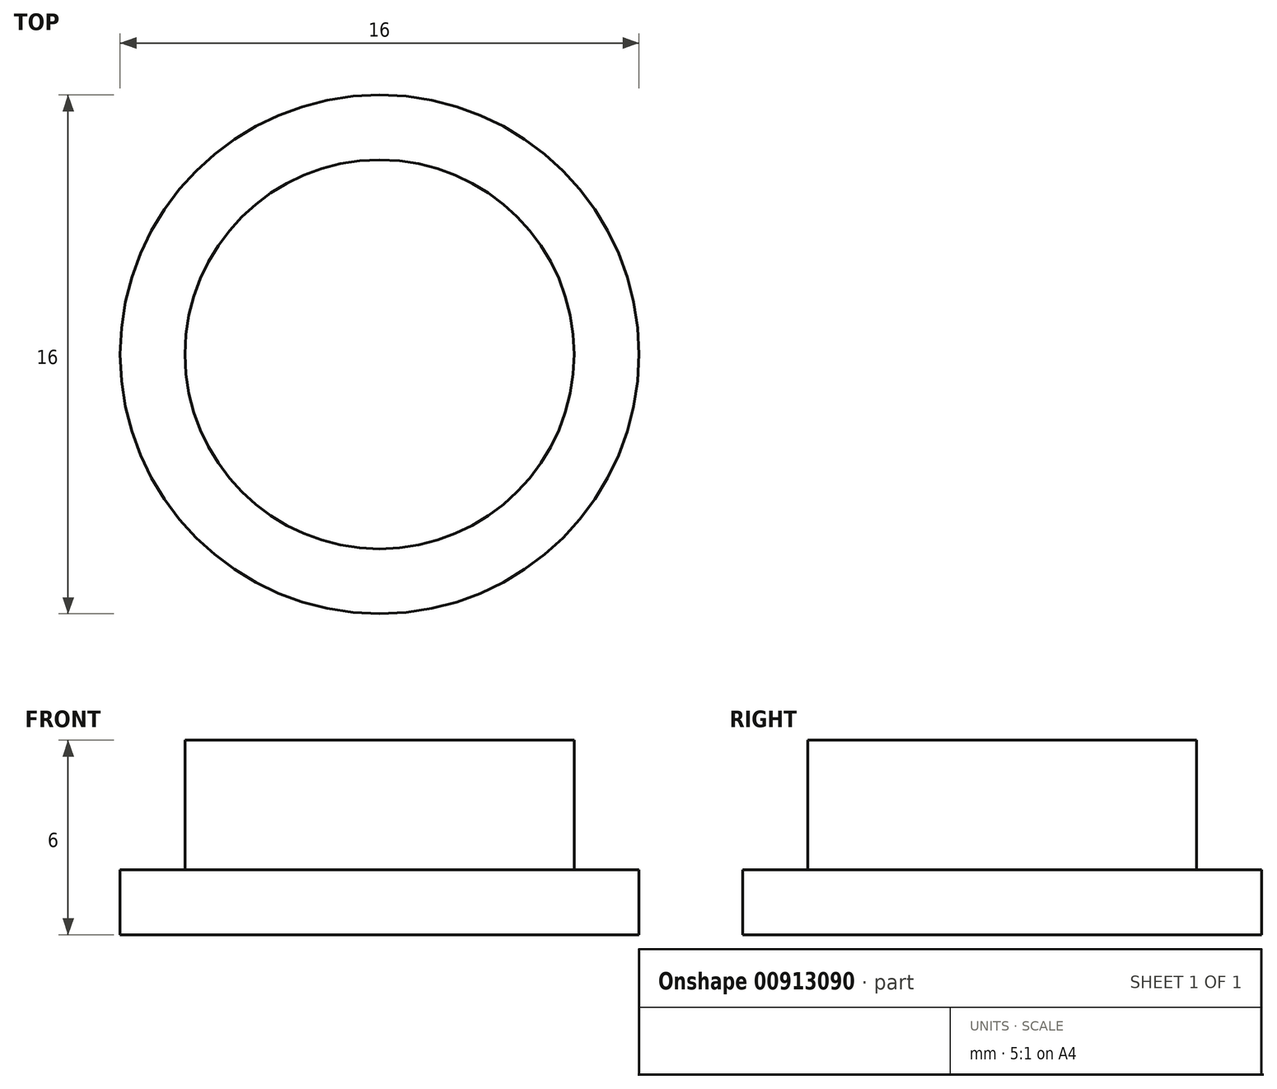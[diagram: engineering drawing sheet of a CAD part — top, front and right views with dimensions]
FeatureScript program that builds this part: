
annotation { "Feature Type Name" : "Feature", "Feature Type Description" : "" }
export const myFeature = defineFeature(function(context is Context, id is Id, definition is map)
    precondition{}
    {
        {
            var Q0;
            Q0=qCreatedBy(makeId("Top.planeOp"),FACE);
            var sketch = newSketch(context, id + "F0", { "sketchPlane" : qUnion([Q0])});
            skCircle(sketch, "E0", {"center": v(0, 0) * mm, "radius": 6 * mm});
            skCircle(sketch, "E1", {"center": v(0, 0) * mm, "radius": 8 * mm});
            skSolve(sketch);
        }
        {
            var Q0;
            Q0=makeQuery(id+"F0.imprint","IMPRINT",FACE,{"disambiguationData":[TD([[makeQuery(id+"F0.imprint","IMPRINT",EDGE,{"derivedFrom":sQuery(id+"F0.wireOp",EDGE,"E0")}),1.0]])]});
            extrude(context, id + "F1", {"entities" : qUnion([Q0]), "depth" : 4 * mm, "offsetDistance" : 25 * mm});
        }
        {
            var Q0;
            Q0 = qSketchRegion(id + "F0", true);
            var Q1;
            Q1=makeQuery(id+"F0.imprint","IMPRINT",FACE,{"disambiguationData":[TD([[makeQuery(id+"F0.imprint","IMPRINT",EDGE,{"derivedFrom":sQuery(id+"F0.wireOp",EDGE,"E0")}),1.0]])]});
            extrude(context, id + "F2", {"entities" : qUnion([Q0, Q1]), "operationType" : NewBodyOperationType.ADD, "oppositeDirection" : true, "depth" : 2 * mm, "offsetDistance" : 25 * mm});
        }
    });
